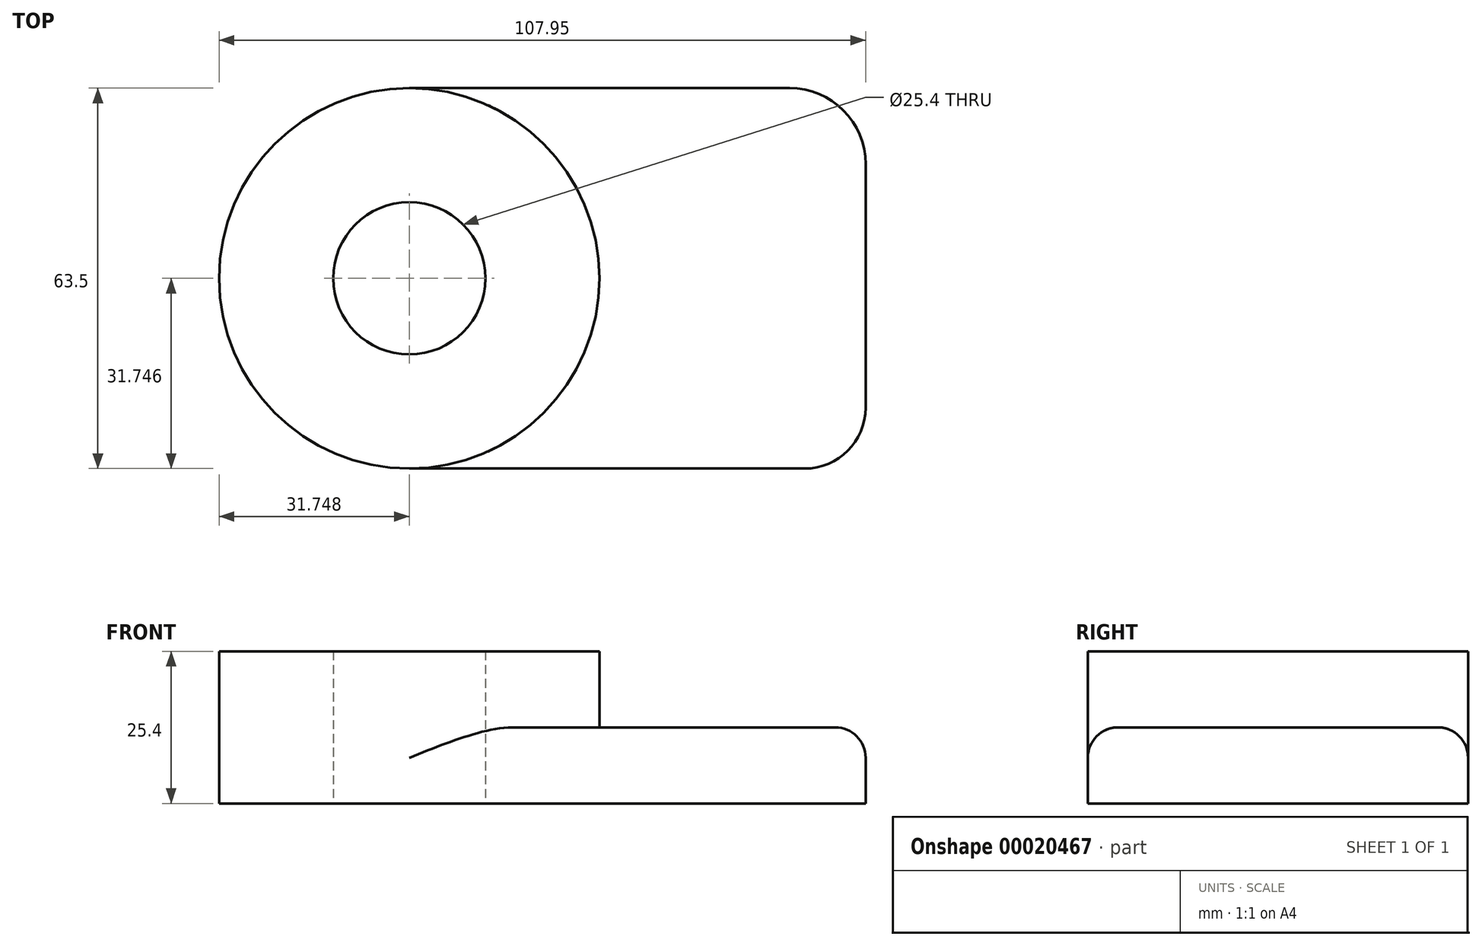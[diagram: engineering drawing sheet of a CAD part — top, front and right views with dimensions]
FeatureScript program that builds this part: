
annotation { "Feature Type Name" : "Feature", "Feature Type Description" : "" }
export const myFeature = defineFeature(function(context is Context, id is Id, definition is map)
    precondition{}
    {
        {
            var Q0;
            Q0=qCreatedBy(makeId("Top.planeOp"),FACE);
            var sketch = newSketch(context, id + "F0", { "sketchPlane" : qUnion([Q0])});
            skLineSegment(sketch, "E0.bottom", {"start": v(-38.3, 28.4) * mm, "end": v(37.9, 28.4) * mm});
            skLineSegment(sketch, "E0.top", {"start": v(-38.3, -35.1) * mm, "end": v(37.9, -35.1) * mm});
            skLineSegment(sketch, "E0.left", {"start": v(-38.3, 28.4) * mm, "end": v(-38.3, -35.1) * mm});
            skLineSegment(sketch, "E0.right", {"start": v(37.9, 28.4) * mm, "end": v(37.9, -35.1) * mm});
            skCircle(sketch, "E1", {"center": v(-38.3, -3.34) * mm, "radius": 31.75 * mm});
            skCircle(sketch, "E2", {"center": v(-38.3, -3.34) * mm, "radius": 12.7 * mm});
            skSolve(sketch);
        }
        {
            var Q0;
            Q0 = qSketchRegion(id + "F0", true);
            extrude(context, id + "F1", {"entities" : qUnion([Q0]), "depth" : 12.7 * mm});
        }
        {
            var Q0;
            {var subQ0=sQuery(id+"F0.wireOp",EDGE,"E2");var subQ1=sQuery(id+"F0.wireOp",EDGE,"E0.left");var subQ3=makeQuery(id+"F0.imprint","INTERSECT",VERTEX,{"disambiguationData":[OD(0.0)],"derivedFrom":[subQ1,subQ0]});Q0=makeQuery(id+"F0.imprint","IMPRINT",FACE,{"disambiguationData":[TD([[makeQuery(id+"F0.imprint","IMPRINT",EDGE,{"disambiguationData":[TD([[subQ3,-1.0]])],"derivedFrom":subQ0}),-1.0]])]});}
            var Q1;
            {var subQ0=sQuery(id+"F0.wireOp",EDGE,"E2");var subQ1=sQuery(id+"F0.wireOp",EDGE,"E0.left");var subQ3=makeQuery(id+"F0.imprint","INTERSECT",VERTEX,{"disambiguationData":[OD(0.0)],"derivedFrom":[subQ1,subQ0]});Q1=makeQuery(id+"F0.imprint","IMPRINT",FACE,{"disambiguationData":[TD([[makeQuery(id+"F0.imprint","IMPRINT",EDGE,{"disambiguationData":[TD([[subQ3,1.0]])],"derivedFrom":subQ0}),-1.0]])]});}
            extrude(context, id + "F2", {"entities" : qUnion([Q0, Q1]), "operationType" : NewBodyOperationType.ADD, "depth" : 25.4 * mm});
        }
        {
            var Q0;
            Q0=makeQuery(id+"F1.opExtrude","SWEPT_EDGE",EDGE,{"disambiguationData":[OSD([sQuery(id+"F0.wireOp",EDGE,"E0.top"),sQuery(id+"F0.wireOp",EDGE,"E0.right")])]});
            fillet(context, id + "F3", {"entities" : qUnion([Q0]), "radius" : 10.16 * mm, "tangentPropagation" : true, "allowEdgeOverflow" : false});
        }
        {
            var Q0;
            Q0=makeQuery(id+"F1.opExtrude","SWEPT_EDGE",EDGE,{"disambiguationData":[OSD([sQuery(id+"F0.wireOp",EDGE,"E0.bottom"),sQuery(id+"F0.wireOp",EDGE,"E0.right")])]});
            fillet(context, id + "F4", {"entities" : qUnion([Q0]), "radius" : 12.7 * mm, "tangentPropagation" : true, "allowEdgeOverflow" : false});
        }
        {
            var Q0;
            Q0=makeQuery(id+"F1.opExtrude","CAP_EDGE",EDGE,{"disambiguationData":[OSD([sQuery(id+"F0.wireOp",EDGE,"E0.right")])],"isStart":false});
            var Q1;
            {var subQ0=sQuery(id+"F0.wireOp",EDGE,"E0.top");var subQ1=sQuery(id+"F0.wireOp",EDGE,"E0.right");Q1=makeQuery(id+"F3.opFillet","BLEND_EDGE",EDGE,{"blendedFrom":[makeQuery(id+"F1.opExtrude","SWEPT_EDGE",EDGE,{"disambiguationData":[OSD([subQ0,subQ1])]}),makeQuery(id+"F1.opExtrude","CAP_FACE",FACE,{"disambiguationData":[OSD([sQuery(id+"F0.wireOp",EDGE,"E0.bottom"),subQ0,subQ1,sQuery(id+"F0.wireOp",EDGE,"E1"),sQuery(id+"F0.wireOp",EDGE,"E2")])],"isStart":false})],"blendedInto":[makeQuery(id+"F1.opExtrude","CAP_FACE",FACE,{"disambiguationData":[OSD([sQuery(id+"F0.wireOp",EDGE,"E0.bottom"),subQ0,subQ1,sQuery(id+"F0.wireOp",EDGE,"E1"),sQuery(id+"F0.wireOp",EDGE,"E2")])],"isStart":false})]});}
            var Q2;
            {var subQ0=sQuery(id+"F0.wireOp",EDGE,"E0.bottom");var subQ1=sQuery(id+"F0.wireOp",EDGE,"E0.right");Q2=makeQuery(id+"F4.opFillet","BLEND_EDGE",EDGE,{"blendedFrom":[makeQuery(id+"F1.opExtrude","SWEPT_EDGE",EDGE,{"disambiguationData":[OSD([subQ0,subQ1])]}),makeQuery(id+"F1.opExtrude","CAP_FACE",FACE,{"disambiguationData":[OSD([subQ0,sQuery(id+"F0.wireOp",EDGE,"E0.top"),subQ1,sQuery(id+"F0.wireOp",EDGE,"E1"),sQuery(id+"F0.wireOp",EDGE,"E2")])],"isStart":false})],"blendedInto":[makeQuery(id+"F1.opExtrude","CAP_FACE",FACE,{"disambiguationData":[OSD([subQ0,sQuery(id+"F0.wireOp",EDGE,"E0.top"),subQ1,sQuery(id+"F0.wireOp",EDGE,"E1"),sQuery(id+"F0.wireOp",EDGE,"E2")])],"isStart":false})]});}
            fillet(context, id + "F5", {"entities" : qUnion([Q0, Q1, Q2]), "radius" : 5.08 * mm, "tangentPropagation" : true, "allowEdgeOverflow" : false});
        }
    });
